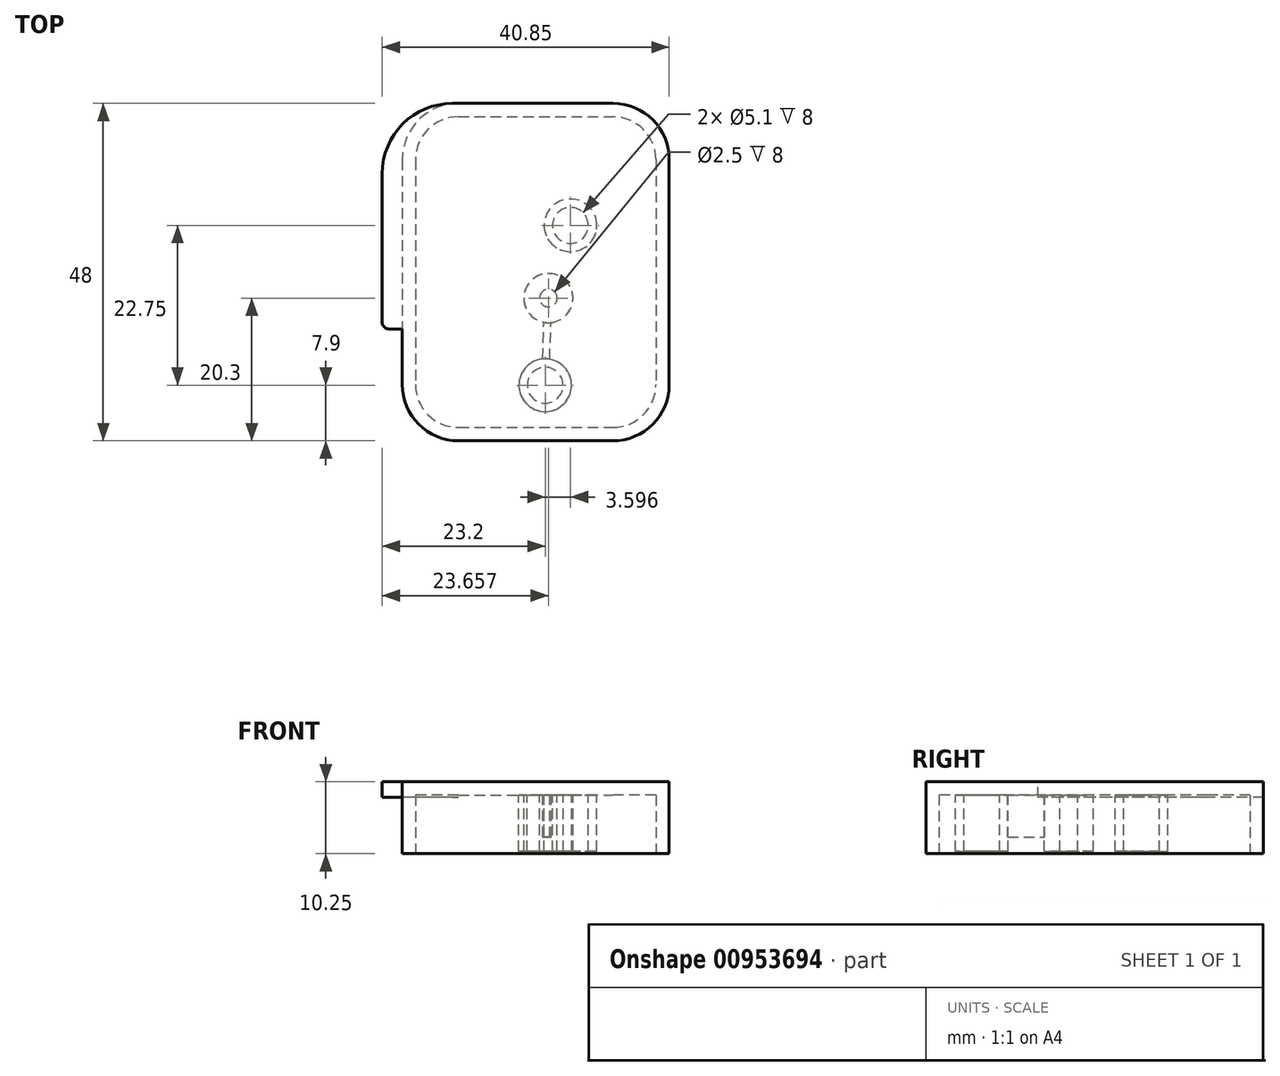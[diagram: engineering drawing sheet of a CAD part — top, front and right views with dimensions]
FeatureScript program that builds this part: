
annotation { "Feature Type Name" : "Feature", "Feature Type Description" : "" }
export const myFeature = defineFeature(function(context is Context, id is Id, definition is map)
    precondition{}
    {
        {
            var Q0;
            Q0=qCreatedBy(makeId("Top.planeOp"),FACE);
            var sketch = newSketch(context, id + "F0", { "sketchPlane" : qUnion([Q0])});
            skLineSegment(sketch, "E0.bottom", {"start": v(-11, 24) * mm, "end": v(11, 24) * mm});
            skLineSegment(sketch, "E0.top", {"start": v(-11, -24) * mm, "end": v(11, -24) * mm});
            skLineSegment(sketch, "E0.left", {"start": v(-19, 16) * mm, "end": v(-19, -16) * mm});
            skLineSegment(sketch, "E0.right", {"start": v(19, 16) * mm, "end": v(19, -16) * mm});
            skPoint(sketch, "E1.visualSharp", {"position": v(-19, 24) * mm});
            skArc(sketch, "E1.filletArc", {"start": v(-11, 24) * mm, "mid": v(-16.66, 21.66) * mm, "end": v(-19, 16) * mm});
            skPoint(sketch, "E2.visualSharp", {"position": v(19, 24) * mm});
            skArc(sketch, "E2.filletArc", {"start": v(19, 16) * mm, "mid": v(16.66, 21.66) * mm, "end": v(11, 24) * mm});
            skPoint(sketch, "E3.visualSharp", {"position": v(19, -24) * mm});
            skArc(sketch, "E3.filletArc", {"start": v(11, -24) * mm, "mid": v(16.66, -21.66) * mm, "end": v(19, -16) * mm});
            skPoint(sketch, "E4.visualSharp", {"position": v(-19, -24) * mm});
            skArc(sketch, "E4.filletArc", {"start": v(-19, -16) * mm, "mid": v(-16.66, -21.66) * mm, "end": v(-11, -24) * mm});
            skSolve(sketch);
        }
        {
            var Q0;
            Q0=makeQuery(id+"F0.imprint","IMPRINT",FACE,{"disambiguationData":[TD([[makeQuery(id+"F0.imprint","IMPRINT",EDGE,{"derivedFrom":sQuery(id+"F0.wireOp",EDGE,"E0.bottom")}),-1.0]])]});
            extrude(context, id + "F1", {"entities" : qUnion([Q0]), "depth" : 10.25 * mm, "offsetDistance" : 25 * mm});
        }
        {
            var Q0;
            Q0=makeQuery(id+"F1.opExtrude","CAP_FACE",FACE,{"disambiguationData":[OSD([sQuery(id+"F0.wireOp",EDGE,"E0.bottom"),sQuery(id+"F0.wireOp",EDGE,"E0.top"),sQuery(id+"F0.wireOp",EDGE,"E0.left"),sQuery(id+"F0.wireOp",EDGE,"E0.right"),sQuery(id+"F0.wireOp",EDGE,"E1.filletArc"),sQuery(id+"F0.wireOp",EDGE,"E2.filletArc"),sQuery(id+"F0.wireOp",EDGE,"E3.filletArc"),sQuery(id+"F0.wireOp",EDGE,"E4.filletArc")])],"isStart":false});
            var sketch = newSketch(context, id + "F2", { "sketchPlane" : qUnion([Q0])});
            skLineSegment(sketch, "E5", {"start": v(21.85, 15.2) * mm, "end": v(21.85, -8.1) * mm});
            skLineSegment(sketch, "E6", {"start": v(-11, 24) * mm, "end": v(11, 24) * mm});
            skLineSegment(sketch, "E7.bottom", {"start": v(-11.85, 24) * mm, "end": v(11.85, 24) * mm});
            skLineSegment(sketch, "E7.top", {"start": v(-21.85, -8.1) * mm, "end": v(21.85, -8.1) * mm});
            skLineSegment(sketch, "E7.left", {"start": v(-21.85, 14) * mm, "end": v(-21.85, -8.1) * mm});
            skLineSegment(sketch, "E7.right", {"start": v(21.85, 14) * mm, "end": v(21.85, -5.8) * mm});
            skPoint(sketch, "E8.visualSharp", {"position": v(-21.85, 24) * mm});
            skArc(sketch, "E8.filletArc", {"start": v(-11.85, 24) * mm, "mid": v(-18.92, 21.07) * mm, "end": v(-21.85, 14) * mm});
            skPoint(sketch, "E9.visualSharp", {"position": v(21.85, 24) * mm});
            skArc(sketch, "E9.filletArc", {"start": v(21.85, 14) * mm, "mid": v(18.92, 21.07) * mm, "end": v(11.85, 24) * mm});
            skSolve(sketch);
        }
        {
            var Q0;
            {var subQ1=sQuery(id+"F2.wireOp",EDGE,"E7.left");Q0=makeQuery(id+"F2.imprint","IMPRINT",FACE,{"disambiguationData":[TD([[makeQuery(id+"F2.imprint","IMPRINT",EDGE,{"derivedFrom":subQ1}),1.0]])]});}
            var Q1;
            {var subQ5=sQuery(id+"F2.wireOp",EDGE,"E7.right");Q1=makeQuery(id+"F2.imprint","IMPRINT",FACE,{"disambiguationData":[TD([[makeQuery(id+"F2.imprint","IMPRINT",EDGE,{"derivedFrom":subQ5}),-1.0]])]});}
            extrude(context, id + "F3", {"entities" : qUnion([Q0, Q1]), "operationType" : NewBodyOperationType.ADD, "oppositeDirection" : true, "depth" : 2.25 * mm, "offsetDistance" : 25 * mm});
        }
        {
            var Q0;
            Q0=makeQuery(id+"F3.opExtrude","SWEPT_EDGE",EDGE,{"disambiguationData":[OSD([sQuery(id+"F2.wireOp",EDGE,"E5"),sQuery(id+"F2.wireOp",EDGE,"E7.top")])]});
            var Q1;
            Q1=makeQuery(id+"F3.opExtrude","SWEPT_EDGE",EDGE,{"disambiguationData":[OSD([sQuery(id+"F0.wireOp",EDGE,"E0.right"),sQuery(id+"F2.wireOp",EDGE,"E7.top")])]});
            var Q2;
            Q2=makeQuery(id+"F3.opExtrude","SWEPT_EDGE",EDGE,{"disambiguationData":[OSD([sQuery(id+"F2.wireOp",EDGE,"E7.top"),sQuery(id+"F2.wireOp",EDGE,"E7.left")])]});
            var Q3;
            Q3=makeQuery(id+"F3.opExtrude","SWEPT_EDGE",EDGE,{"disambiguationData":[OSD([sQuery(id+"F0.wireOp",EDGE,"E0.left"),sQuery(id+"F2.wireOp",EDGE,"E7.top")])]});
            fillet(context, id + "F4", {"entities" : qUnion([Q0, Q1, Q2, Q3]), "radius" : 1 * mm, "tangentPropagation" : true, "allowEdgeOverflow" : false});
        }
        {
            var Q0;
            Q0=makeQuery(id+"F1.opExtrude","CAP_FACE",FACE,{"disambiguationData":[OSD([sQuery(id+"F0.wireOp",EDGE,"E0.bottom"),sQuery(id+"F0.wireOp",EDGE,"E0.top"),sQuery(id+"F0.wireOp",EDGE,"E0.left"),sQuery(id+"F0.wireOp",EDGE,"E0.right"),sQuery(id+"F0.wireOp",EDGE,"E1.filletArc"),sQuery(id+"F0.wireOp",EDGE,"E2.filletArc"),sQuery(id+"F0.wireOp",EDGE,"E3.filletArc"),sQuery(id+"F0.wireOp",EDGE,"E4.filletArc")])],"isStart":true});
            shell(context, id + "F5", {"entities" : qUnion([Q0]), "thickness" : 1.9 * mm});
        }
        {
            var Q0;
            Q0=makeQuery(id+"F5.opShell","OFFSET_FACE",FACE,{"disambiguationData":[OSD([sQuery(id+"F0.wireOp",EDGE,"E0.bottom"),sQuery(id+"F0.wireOp",EDGE,"E0.top"),sQuery(id+"F0.wireOp",EDGE,"E0.left"),sQuery(id+"F0.wireOp",EDGE,"E0.right"),sQuery(id+"F0.wireOp",EDGE,"E1.filletArc"),sQuery(id+"F0.wireOp",EDGE,"E2.filletArc"),sQuery(id+"F0.wireOp",EDGE,"E3.filletArc"),sQuery(id+"F0.wireOp",EDGE,"E4.filletArc"),sQuery(id+"F2.wireOp",EDGE,"E5"),sQuery(id+"F2.wireOp",EDGE,"E7.bottom"),sQuery(id+"F2.wireOp",EDGE,"E7.top"),sQuery(id+"F2.wireOp",EDGE,"E7.left"),sQuery(id+"F2.wireOp",EDGE,"E7.right"),sQuery(id+"F2.wireOp",EDGE,"E8.filletArc"),sQuery(id+"F2.wireOp",EDGE,"E9.filletArc")])]});
            var sketch = newSketch(context, id + "F6", { "sketchPlane" : qUnion([Q0])});
            skCircle(sketch, "E10", {"center": v(1.35, 16.1) * mm, "radius": 3.75 * mm});
            skCircle(sketch, "E11", {"center": v(1.35, 16.1) * mm, "radius": 2.55 * mm});
            skSolve(sketch);
        }
        {
            var Q0;
            Q0=makeQuery(id+"F6.imprint","IMPRINT",FACE,{"disambiguationData":[TD([[makeQuery(id+"F6.imprint","IMPRINT",EDGE,{"derivedFrom":sQuery(id+"F6.wireOp",EDGE,"E10")}),1.0]])]});
            extrude(context, id + "F7", {"entities" : qUnion([Q0]), "operationType" : NewBodyOperationType.ADD, "depth" : 8 * mm, "offsetDistance" : 25 * mm});
        }
        {
            var Q0;
            {var subQ0=sQuery(id+"F2.wireOp",EDGE,"E7.bottom");var subQ1=sQuery(id+"F0.wireOp",EDGE,"E0.bottom");var subQ2=sQuery(id+"F0.wireOp",EDGE,"E4.filletArc");var subQ3=sQuery(id+"F0.wireOp",EDGE,"E3.filletArc");var subQ4=sQuery(id+"F0.wireOp",EDGE,"E0.top");var subQ5=sQuery(id+"F0.wireOp",EDGE,"E1.filletArc");var subQ6=sQuery(id+"F0.wireOp",EDGE,"E2.filletArc");var subQ7=sQuery(id+"F0.wireOp",EDGE,"E0.left");var subQ8=sQuery(id+"F0.wireOp",EDGE,"E0.right");Q0=makeQuery(id+"F7.boolean.opBoolean","SPLIT",FACE,{"disambiguationData":[TD([makeQuery(id+"F5.opShell","OFFSET_FACE",FACE,{"disambiguationData":[OSD([subQ4])]})])],"derivedFrom":makeQuery(id+"F5.opShell","OFFSET_FACE",FACE,{"disambiguationData":[OSD([subQ1,subQ4,subQ7,subQ8,subQ5,subQ6,subQ3,subQ2,sQuery(id+"F2.wireOp",EDGE,"E5"),subQ0,sQuery(id+"F2.wireOp",EDGE,"E7.top"),sQuery(id+"F2.wireOp",EDGE,"E7.left"),sQuery(id+"F2.wireOp",EDGE,"E7.right"),sQuery(id+"F2.wireOp",EDGE,"E8.filletArc"),sQuery(id+"F2.wireOp",EDGE,"E9.filletArc")])]})});}
            var sketch = newSketch(context, id + "F8", { "sketchPlane" : qUnion([Q0])});
            skCircle(sketch, "E12", {"center": v(1.8, 3.7) * mm, "radius": 3.5 * mm});
            skCircle(sketch, "E13", {"center": v(1.8, 3.7) * mm, "radius": 1.25 * mm});
            skSolve(sketch);
        }
        {
            var Q0;
            Q0 = qSketchRegion(id + "F8", true);
            extrude(context, id + "F9", {"entities" : qUnion([Q0]), "operationType" : NewBodyOperationType.ADD, "depth" : 8 * mm, "offsetDistance" : 25 * mm});
        }
        {
            var Q0;
            {var subQ0=sQuery(id+"F2.wireOp",EDGE,"E7.bottom");var subQ1=sQuery(id+"F0.wireOp",EDGE,"E0.bottom");var subQ3=sQuery(id+"F0.wireOp",EDGE,"E4.filletArc");var subQ5=sQuery(id+"F0.wireOp",EDGE,"E3.filletArc");var subQ8=sQuery(id+"F0.wireOp",EDGE,"E0.top");var subQ9=makeQuery(id+"F5.opShell","OFFSET_FACE",FACE,{"disambiguationData":[OSD([subQ8])]});var subQ10=sQuery(id+"F0.wireOp",EDGE,"E1.filletArc");var subQ12=sQuery(id+"F0.wireOp",EDGE,"E2.filletArc");var subQ14=sQuery(id+"F0.wireOp",EDGE,"E0.left");var subQ16=sQuery(id+"F0.wireOp",EDGE,"E0.right");Q0=makeQuery(id+"F9.boolean.opBoolean","SPLIT",FACE,{"disambiguationData":[TD([subQ9])],"derivedFrom":makeQuery(id+"F7.boolean.opBoolean","SPLIT",FACE,{"disambiguationData":[TD([subQ9])],"derivedFrom":makeQuery(id+"F5.opShell","OFFSET_FACE",FACE,{"disambiguationData":[OSD([subQ1,subQ8,subQ14,subQ16,subQ10,subQ12,subQ5,subQ3,sQuery(id+"F2.wireOp",EDGE,"E5"),subQ0,sQuery(id+"F2.wireOp",EDGE,"E7.top"),sQuery(id+"F2.wireOp",EDGE,"E7.left"),sQuery(id+"F2.wireOp",EDGE,"E7.right"),sQuery(id+"F2.wireOp",EDGE,"E8.filletArc"),sQuery(id+"F2.wireOp",EDGE,"E9.filletArc")])]})})});}
            var sketch = newSketch(context, id + "F10", { "sketchPlane" : qUnion([Q0])});
            skCircle(sketch, "E14", {"center": v(4.95, -6.65) * mm, "radius": 3.75 * mm});
            skCircle(sketch, "E15", {"center": v(4.95, -6.65) * mm, "radius": 2.55 * mm});
            skSolve(sketch);
        }
        {
            var Q0;
            Q0 = qSketchRegion(id + "F10", true);
            extrude(context, id + "F11", {"entities" : qUnion([Q0]), "operationType" : NewBodyOperationType.ADD, "depth" : 8 * mm, "offsetDistance" : 25 * mm});
        }
        {
            var Q0;
            {var subQ1=sQuery(id+"F0.wireOp",EDGE,"E0.right");var subQ3=sQuery(id+"F0.wireOp",EDGE,"E0.left");var subQ5=sQuery(id+"F0.wireOp",EDGE,"E2.filletArc");var subQ7=sQuery(id+"F0.wireOp",EDGE,"E1.filletArc");var subQ10=sQuery(id+"F0.wireOp",EDGE,"E0.top");var subQ11=makeQuery(id+"F5.opShell","OFFSET_FACE",FACE,{"disambiguationData":[OSD([subQ10])]});var subQ12=sQuery(id+"F0.wireOp",EDGE,"E3.filletArc");var subQ14=sQuery(id+"F0.wireOp",EDGE,"E4.filletArc");var subQ16=sQuery(id+"F2.wireOp",EDGE,"E7.bottom");var subQ17=sQuery(id+"F0.wireOp",EDGE,"E0.bottom");Q0=makeQuery(id+"F11.boolean.opBoolean","SPLIT",FACE,{"disambiguationData":[TD([subQ11])],"derivedFrom":makeQuery(id+"F9.boolean.opBoolean","SPLIT",FACE,{"disambiguationData":[TD([subQ11])],"derivedFrom":makeQuery(id+"F7.boolean.opBoolean","SPLIT",FACE,{"disambiguationData":[TD([subQ11])],"derivedFrom":makeQuery(id+"F5.opShell","OFFSET_FACE",FACE,{"disambiguationData":[OSD([subQ17,subQ10,subQ3,subQ1,subQ7,subQ5,subQ12,subQ14,sQuery(id+"F2.wireOp",EDGE,"E5"),subQ16,sQuery(id+"F2.wireOp",EDGE,"E7.top"),sQuery(id+"F2.wireOp",EDGE,"E7.left"),sQuery(id+"F2.wireOp",EDGE,"E7.right"),sQuery(id+"F2.wireOp",EDGE,"E8.filletArc"),sQuery(id+"F2.wireOp",EDGE,"E9.filletArc")])]})})})});}
            var sketch = newSketch(context, id + "F12", { "sketchPlane" : qUnion([Q0])});
            skArc(sketch, "E16.0", {"start": v(11, -27.1) * mm, "mid": v(18.85, -23.85) * mm, "end": v(22.1, -16) * mm});
            skLineSegment(sketch, "E16.1", {"start": v(-11, -27.1) * mm, "end": v(11, -27.1) * mm});
            skLineSegment(sketch, "E16.2", {"start": v(22.1, -16) * mm, "end": v(22.1, 16) * mm});
            skArc(sketch, "E16.3", {"start": v(-22.1, -16) * mm, "mid": v(-18.85, -23.85) * mm, "end": v(-11, -27.1) * mm});
            skArc(sketch, "E16.4", {"start": v(22.1, 16) * mm, "mid": v(18.85, 23.85) * mm, "end": v(11, 27.1) * mm});
            skLineSegment(sketch, "E16.5", {"start": v(11, 27.1) * mm, "end": v(-11, 27.1) * mm});
            skArc(sketch, "E16.6", {"start": v(-11, 27.1) * mm, "mid": v(-18.85, 23.85) * mm, "end": v(-22.1, 16) * mm});
            skLineSegment(sketch, "E16.7", {"start": v(-22.1, 16) * mm, "end": v(-22.1, -16) * mm});
            skLineSegment(sketch, "E17", {"start": v(0.99, 12.37) * mm, "end": v(1.18, 7.14) * mm});
            skLineSegment(sketch, "E18", {"start": v(1.99, 12.4) * mm, "end": v(2.18, 7.18) * mm});
            skArc(sketch, "E19", {"start": v(1.18, 7.14) * mm, "mid": v(1.68, 7.2) * mm, "end": v(2.18, 7.18) * mm});
            skArc(sketch, "E20", {"start": v(0.99, 12.37) * mm, "mid": v(1.49, 12.35) * mm, "end": v(1.99, 12.4) * mm});
            skSolve(sketch);
        }
        {
            var Q0;
            Q0=makeQuery(id+"F12.imprint","IMPRINT",FACE,{"disambiguationData":[TD([[makeQuery(id+"F12.imprint","IMPRINT",EDGE,{"derivedFrom":sQuery(id+"F12.wireOp",EDGE,"E17")}),1.0]])]});
            extrude(context, id + "F13", {"entities" : qUnion([Q0]), "operationType" : NewBodyOperationType.ADD, "depth" : 6 * mm, "offsetDistance" : 25 * mm});
        }
    });
